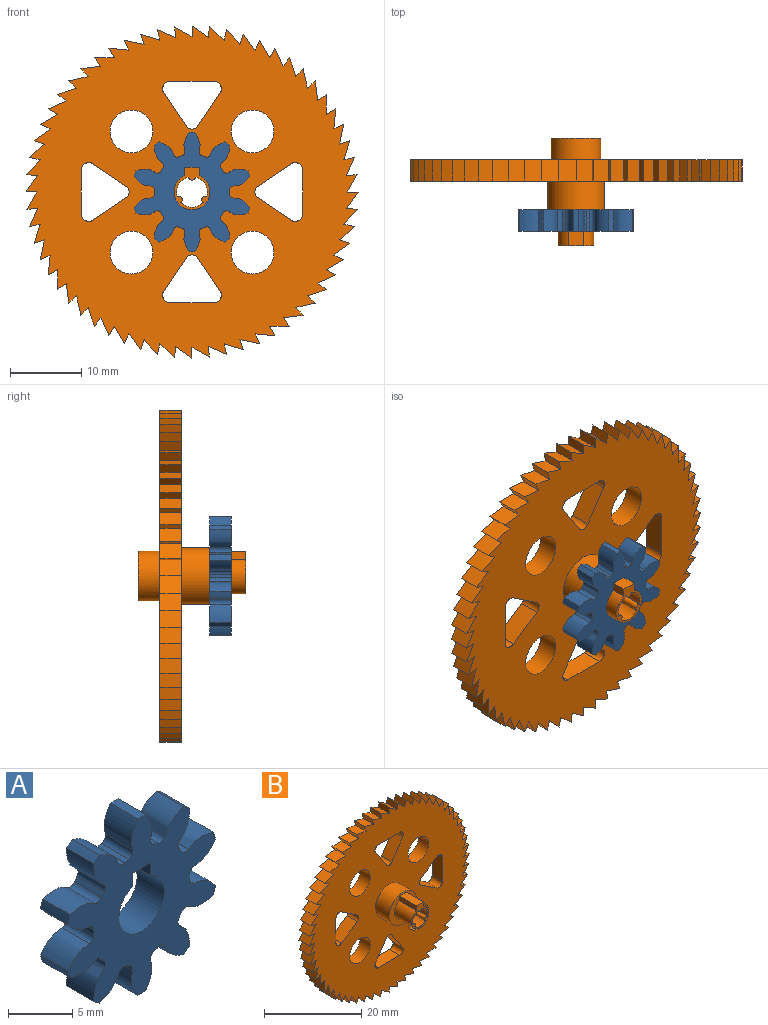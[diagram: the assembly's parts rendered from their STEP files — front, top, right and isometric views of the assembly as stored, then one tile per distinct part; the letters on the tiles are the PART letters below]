
ASSEMBLY  parts=2 mates=1
PART A: 66 faces, bbox 16.2x3x16.8 mm
  f0: cylinder r=8.4mm len=3mm, axis (0,1,0), area 2.5mm2, adj f9,f15,f56,f63
  f1: cylinder r=8.4mm len=3mm, axis (0,1,0), area 2.5mm2, adj f9,f15,f16,f58
  f2: cylinder r=8.4mm len=3mm, axis (0,1,0), area 2.5mm2, adj f9,f15,f46,f53
  f3: cylinder r=8.4mm len=3mm, axis (0,1,0), area 2.5mm2, adj f9,f15,f48,f61
  f4: cylinder r=8.4mm len=3mm, axis (0,1,0), area 2.5mm2, adj f9,f15,f36,f43
  f5: cylinder r=8.4mm len=3mm, axis (0,1,0), area 2.5mm2, adj f9,f15,f31,f38
  f6: cylinder r=8.4mm len=3mm, axis (0,1,0), area 2.5mm2, adj f9,f15,f26,f33
  f7: cylinder r=8.4mm len=3mm, axis (0,1,0), area 2.5mm2, adj f9,f15,f28,f51
  f8: cylinder r=8.4mm len=3mm, axis (0,1,0), area 2.5mm2, adj f9,f15,f23,f41
  f9: plane 16.83x16.25mm, normal (0,-1,0), area 125.5mm2, adj f0,f1,f2,f3,f4,f5,f6,f7
  f10: plane 3x1.21mm, normal (-1,0,0), area 3.6mm2, adj f9,f11,f13,f15
  f11: cylinder r=2.5mm len=5mm, axis (0,1,0), area 41mm2, adj f9,f10,f12,f15
  f12: plane 3x1.21mm, normal (1,0,0), area 3.6mm2, adj f9,f11,f13,f15
  f13: plane 3x2mm, normal (0,0,-1), area 6mm2, adj f9,f10,f12,f15
  f14: cylinder r=8.4mm len=3mm, axis (0,1,0), area 2.5mm2, adj f9,f15,f18,f21
  f15: plane 16.83x16.25mm, normal (0,1,0), area 125.5mm2, adj f0,f1,f2,f3,f4,f5,f6,f7
  f16: extruded ~3x2.37mm, area 8.5mm2, adj f1,f9,f15,f19
  f17: cylinder r=5.25mm len=3mm, axis (0,1,0), area 1.3mm2, adj f9,f15,f19,f20
  f18: extruded ~3x2.37mm, area 8.5mm2, adj f9,f14,f15,f20
  f19: cylinder r=0.58mm len=3mm, axis (0,1,0), area 2.5mm2, adj f9,f15,f16,f17
  f20: cylinder r=0.58mm len=3mm, axis (0,1,0), area 2.5mm2, adj f9,f15,f17,f18
  f21: extruded ~3x2.73mm, area 8.5mm2, adj f9,f14,f15,f24
  f22: cylinder r=5.25mm len=3mm, axis (0,1,0), area 1.3mm2, adj f9,f15,f24,f25
  f23: extruded ~3x2.51mm, area 8.5mm2, adj f8,f9,f15,f25
  f24: cylinder r=0.58mm len=3mm, axis (0,1,0), area 2.5mm2, adj f9,f15,f21,f22
  f25: cylinder r=0.58mm len=3mm, axis (0,1,0), area 2.5mm2, adj f9,f15,f22,f23
  f26: extruded ~3x2.37mm, area 8.5mm2, adj f6,f9,f15,f29
  f27: cylinder r=5.25mm len=3mm, axis (0,1,0), area 1.3mm2, adj f9,f15,f29,f30
  f28: extruded ~3x2.37mm, area 8.5mm2, adj f7,f9,f15,f30
  f29: cylinder r=0.58mm len=3mm, axis (0,1,0), area 2.5mm2, adj f9,f15,f26,f27
  f30: cylinder r=0.58mm len=3mm, axis (0,1,0), area 2.5mm2, adj f9,f15,f27,f28
  f31: extruded ~3x2.51mm, area 8.5mm2, adj f5,f9,f15,f34
  f32: cylinder r=5.25mm len=3mm, axis (0,1,0), area 1.3mm2, adj f9,f15,f34,f35
  f33: extruded ~3x2.73mm, area 8.5mm2, adj f6,f9,f15,f35
  f34: cylinder r=0.58mm len=3mm, axis (0,1,0), area 2.5mm2, adj f9,f15,f31,f32
  f35: cylinder r=0.58mm len=3mm, axis (0,1,0), area 2.5mm2, adj f9,f15,f32,f33
  f36: extruded ~3x2.68mm, area 8.5mm2, adj f4,f9,f15,f39
  f37: cylinder r=5.25mm len=3mm, axis (0,1,0), area 1.3mm2, adj f9,f15,f39,f40
  f38: extruded ~3x2.05mm, area 8.5mm2, adj f5,f9,f15,f40
  f39: cylinder r=0.58mm len=3mm, axis (0,1,0), area 2.5mm2, adj f9,f15,f36,f37
  f40: cylinder r=0.58mm len=3mm, axis (0,1,0), area 2.5mm2, adj f9,f15,f37,f38
  f41: extruded ~3x2.05mm, area 8.5mm2, adj f8,f9,f15,f44
  f42: cylinder r=5.25mm len=3mm, axis (0,1,0), area 1.3mm2, adj f9,f15,f44,f45
  f43: extruded ~3x2.68mm, area 8.5mm2, adj f4,f9,f15,f45
  f44: cylinder r=0.58mm len=3mm, axis (0,1,0), area 2.5mm2, adj f9,f15,f41,f42
  f45: cylinder r=0.58mm len=3mm, axis (0,1,0), area 2.5mm2, adj f9,f15,f42,f43
  f46: extruded ~3x2.05mm, area 8.5mm2, adj f2,f9,f15,f49
  f47: cylinder r=5.25mm len=3mm, axis (0,1,0), area 1.3mm2, adj f9,f15,f49,f50
  f48: extruded ~3x2.68mm, area 8.5mm2, adj f3,f9,f15,f50
  f49: cylinder r=0.58mm len=3mm, axis (0,1,0), area 2.5mm2, adj f9,f15,f46,f47
  f50: cylinder r=0.58mm len=3mm, axis (0,1,0), area 2.5mm2, adj f9,f15,f47,f48
  f51: extruded ~3x2.73mm, area 8.5mm2, adj f7,f9,f15,f54
  f52: cylinder r=5.25mm len=3mm, axis (0,1,0), area 1.3mm2, adj f9,f15,f54,f55
  f53: extruded ~3x2.51mm, area 8.5mm2, adj f2,f9,f15,f55
  f54: cylinder r=0.58mm len=3mm, axis (0,1,0), area 2.5mm2, adj f9,f15,f51,f52
  f55: cylinder r=0.58mm len=3mm, axis (0,1,0), area 2.5mm2, adj f9,f15,f52,f53
  f56: extruded ~3x2.51mm, area 8.5mm2, adj f0,f9,f15,f59
  f57: cylinder r=5.25mm len=3mm, axis (0,1,0), area 1.3mm2, adj f9,f15,f59,f60
  f58: extruded ~3x2.73mm, area 8.5mm2, adj f1,f9,f15,f60
  f59: cylinder r=0.58mm len=3mm, axis (0,1,0), area 2.5mm2, adj f9,f15,f56,f57
  f60: cylinder r=0.58mm len=3mm, axis (0,1,0), area 2.5mm2, adj f9,f15,f57,f58
  f61: extruded ~3x2.68mm, area 8.5mm2, adj f3,f9,f15,f64
  f62: cylinder r=5.25mm len=3mm, axis (0,1,0), area 1.3mm2, adj f9,f15,f64,f65
  f63: extruded ~3x2.05mm, area 8.5mm2, adj f0,f9,f15,f65
  f64: cylinder r=0.58mm len=3mm, axis (0,1,0), area 2.5mm2, adj f9,f15,f61,f62
  f65: cylinder r=0.58mm len=3mm, axis (0,1,0), area 2.5mm2, adj f9,f15,f62,f63
PART B: 165 faces, bbox 46.5x15x46.5 mm
  f0: plane 46.5x46.5mm, normal (0,-1,0), area 1281.1mm2, adj f2,f3,f4,f5,f6,f7,f8,f9
  f1: plane 46.5x46.5mm, normal (0,1,0), area 1292.9mm2, adj f2,f3,f4,f5,f6,f7,f8,f9
  f2: plane 3x1.49mm, normal (-0.99,0,0.1), area 4.5mm2, adj f0,f1,f3,f121
  f3: plane 3x2.27mm, normal (0.58,0,0.81), area 8.4mm2, adj f0,f1,f2,f4
  f4: plane 3x1.5mm, normal (-1,0,0), area 4.5mm2, adj f0,f1,f3,f5
  f5: plane 3x2.43mm, normal (0.49,0,0.87), area 8.4mm2, adj f0,f1,f4,f6
  f6: plane 3x1.49mm, normal (-0.99,0,-0.1), area 4.5mm2, adj f0,f1,f5,f7
  f7: plane 3x2.56mm, normal (0.4,0,0.92), area 8.4mm2, adj f0,f1,f6,f8
  f8: plane 3x1.47mm, normal (-0.98,0,-0.21), area 4.5mm2, adj f0,f1,f7,f9
  f9: plane 3x2.66mm, normal (0.3,0,0.95), area 8.4mm2, adj f0,f1,f8,f10
  f10: plane 3x1.43mm, normal (-0.95,0,-0.31), area 4.5mm2, adj f0,f1,f9,f11
  f11: plane 3x2.74mm, normal (0.2,0,0.98), area 8.4mm2, adj f0,f1,f10,f12
  f12: plane 3x1.37mm, normal (-0.91,0,-0.41), area 4.5mm2, adj f0,f1,f11,f13
  f13: plane 3x2.78mm, normal (0.1,0,1), area 8.4mm2, adj f0,f1,f12,f14
  f14: plane 3x1.3mm, normal (-0.87,0,-0.5), area 4.5mm2, adj f0,f1,f13,f15
  f15: plane 3x2.79mm, normal (-0.01,0,1), area 8.4mm2, adj f0,f1,f14,f16
  f16: plane 3x1.21mm, normal (-0.81,0,-0.59), area 4.5mm2, adj f0,f1,f15,f17
  f17: plane 3x2.77mm, normal (-0.11,0,0.99), area 8.4mm2, adj f0,f1,f16,f18
  f18: plane 3x1.11mm, normal (-0.74,0,-0.67), area 4.5mm2, adj f0,f1,f17,f19
  f19: plane 3x2.72mm, normal (-0.22,0,0.98), area 8.4mm2, adj f0,f1,f18,f20
  f20: plane 3x1.11mm, normal (-0.67,0,-0.74), area 4.5mm2, adj f0,f1,f19,f21
  f21: plane 3x2.65mm, normal (-0.32,0,0.95), area 8.4mm2, adj f0,f1,f20,f22
  f22: plane 3x1.21mm, normal (-0.59,0,-0.81), area 4.5mm2, adj f0,f1,f21,f23
  f23: plane 3x2.54mm, normal (-0.42,0,0.91), area 8.4mm2, adj f0,f1,f22,f24
  f24: plane 3x1.3mm, normal (-0.5,0,-0.87), area 4.5mm2, adj f0,f1,f23,f25
  f25: plane 3x2.4mm, normal (-0.51,0,0.86), area 8.4mm2, adj f0,f1,f24,f26
  f26: plane 3x1.37mm, normal (-0.41,0,-0.91), area 4.5mm2, adj f0,f1,f25,f27
  f27: plane 3x2.24mm, normal (-0.6,0,0.8), area 8.4mm2, adj f0,f1,f26,f28
  f28: plane 3x1.43mm, normal (-0.31,0,-0.95), area 4.5mm2, adj f0,f1,f27,f29
  f29: plane 3x2.06mm, normal (-0.68,0,0.74), area 8.4mm2, adj f0,f1,f28,f30
  f30: plane 3x1.47mm, normal (-0.21,0,-0.98), area 4.5mm2, adj f0,f1,f29,f31
  f31: plane 3x2.09mm, normal (-0.75,0,0.66), area 8.4mm2, adj f0,f1,f30,f32
  f32: plane 3x1.49mm, normal (-0.1,0,-0.99), area 4.5mm2, adj f0,f1,f31,f33
  f33: plane 3x2.27mm, normal (-0.81,0,0.58), area 8.4mm2, adj f0,f1,f32,f34
  f34: plane 3x1.5mm, normal (0,0,-1), area 4.5mm2, adj f0,f1,f33,f35
  f35: plane 3x2.43mm, normal (-0.87,0,0.49), area 8.4mm2, adj f0,f1,f34,f36
  f36: plane 3x1.49mm, normal (0.1,0,-0.99), area 4.5mm2, adj f0,f1,f35,f37
  f37: plane 3x2.56mm, normal (-0.92,0,0.4), area 8.4mm2, adj f0,f1,f36,f38
  f38: plane 3x1.47mm, normal (0.21,0,-0.98), area 4.5mm2, adj f0,f1,f37,f39
  f39: plane 3x2.66mm, normal (-0.95,0,0.3), area 8.4mm2, adj f0,f1,f38,f40
  f40: plane 3x1.43mm, normal (0.31,0,-0.95), area 4.5mm2, adj f0,f1,f39,f41
  f41: plane 3x2.74mm, normal (-0.98,0,0.2), area 8.4mm2, adj f0,f1,f40,f42
  f42: plane 3x1.37mm, normal (0.41,0,-0.91), area 4.5mm2, adj f0,f1,f41,f43
  f43: plane 3x2.78mm, normal (-1,0,0.1), area 8.4mm2, adj f0,f1,f42,f44
  f44: plane 3x1.3mm, normal (0.5,0,-0.87), area 4.5mm2, adj f0,f1,f43,f45
  f45: plane 3x2.79mm, normal (-1,0,-0.01), area 8.4mm2, adj f0,f1,f44,f46
  f46: plane 3x1.21mm, normal (0.59,0,-0.81), area 4.5mm2, adj f0,f1,f45,f47
  f47: plane 3x2.77mm, normal (-0.99,0,-0.11), area 8.4mm2, adj f0,f1,f46,f48
  f48: plane 3x1.11mm, normal (0.67,0,-0.74), area 4.5mm2, adj f0,f1,f47,f49
  f49: plane 3x2.72mm, normal (-0.98,0,-0.22), area 8.4mm2, adj f0,f1,f48,f50
  f50: plane 3x1.11mm, normal (0.74,0,-0.67), area 4.5mm2, adj f0,f1,f49,f51
  f51: plane 3x2.65mm, normal (-0.95,0,-0.32), area 8.4mm2, adj f0,f1,f50,f52
  f52: plane 3x1.21mm, normal (0.81,0,-0.59), area 4.5mm2, adj f0,f1,f51,f53
  f53: plane 3x2.54mm, normal (-0.91,0,-0.42), area 8.4mm2, adj f0,f1,f52,f54
  f54: plane 3x1.3mm, normal (0.87,0,-0.5), area 4.5mm2, adj f0,f1,f53,f55
  f55: plane 3x2.4mm, normal (-0.86,0,-0.51), area 8.4mm2, adj f0,f1,f54,f56
  f56: plane 3x1.37mm, normal (0.91,0,-0.41), area 4.5mm2, adj f0,f1,f55,f57
  f57: plane 3x2.24mm, normal (-0.8,0,-0.6), area 8.4mm2, adj f0,f1,f56,f58
  f58: plane 3x1.43mm, normal (0.95,0,-0.31), area 4.5mm2, adj f0,f1,f57,f59
  f59: plane 3x2.06mm, normal (-0.74,0,-0.68), area 8.4mm2, adj f0,f1,f58,f60
  f60: plane 3x1.47mm, normal (0.98,0,-0.21), area 4.5mm2, adj f0,f1,f59,f61
  f61: plane 3x2.09mm, normal (-0.66,0,-0.75), area 8.4mm2, adj f0,f1,f60,f62
  f62: plane 3x1.49mm, normal (0.99,0,-0.1), area 4.5mm2, adj f0,f1,f61,f63
  f63: plane 3x2.27mm, normal (-0.58,0,-0.81), area 8.4mm2, adj f0,f1,f62,f64
  f64: plane 3x1.5mm, normal (1,0,0), area 4.5mm2, adj f0,f1,f63,f65
  f65: plane 3x2.43mm, normal (-0.49,0,-0.87), area 8.4mm2, adj f0,f1,f64,f66
  f66: plane 3x1.49mm, normal (0.99,0,0.1), area 4.5mm2, adj f0,f1,f65,f67
  f67: plane 3x2.56mm, normal (-0.4,0,-0.92), area 8.4mm2, adj f0,f1,f66,f68
  f68: plane 3x1.47mm, normal (0.98,0,0.21), area 4.5mm2, adj f0,f1,f67,f69
  f69: plane 3x2.66mm, normal (-0.3,0,-0.95), area 8.4mm2, adj f0,f1,f68,f70
  f70: plane 3x1.43mm, normal (0.95,0,0.31), area 4.5mm2, adj f0,f1,f69,f71
  f71: plane 3x2.74mm, normal (-0.2,0,-0.98), area 8.4mm2, adj f0,f1,f70,f72
  f72: plane 3x1.37mm, normal (0.91,0,0.41), area 4.5mm2, adj f0,f1,f71,f73
  f73: plane 3x2.78mm, normal (-0.1,0,-1), area 8.4mm2, adj f0,f1,f72,f74
  f74: plane 3x1.3mm, normal (0.87,0,0.5), area 4.5mm2, adj f0,f1,f73,f75
  f75: plane 3x2.79mm, normal (0.01,0,-1), area 8.4mm2, adj f0,f1,f74,f76
  f76: plane 3x1.21mm, normal (0.81,0,0.59), area 4.5mm2, adj f0,f1,f75,f77
  f77: plane 3x2.77mm, normal (0.11,0,-0.99), area 8.4mm2, adj f0,f1,f76,f78
  f78: plane 3x1.11mm, normal (0.74,0,0.67), area 4.5mm2, adj f0,f1,f77,f79
  f79: plane 3x2.72mm, normal (0.22,0,-0.98), area 8.4mm2, adj f0,f1,f78,f80
  f80: plane 3x1.11mm, normal (0.67,0,0.74), area 4.5mm2, adj f0,f1,f79,f81
  f81: plane 3x2.65mm, normal (0.32,0,-0.95), area 8.4mm2, adj f0,f1,f80,f82
  f82: plane 3x1.21mm, normal (0.59,0,0.81), area 4.5mm2, adj f0,f1,f81,f83
  f83: plane 3x2.54mm, normal (0.42,0,-0.91), area 8.4mm2, adj f0,f1,f82,f84
  f84: plane 3x1.3mm, normal (0.5,0,0.87), area 4.5mm2, adj f0,f1,f83,f85
  f85: plane 3x2.4mm, normal (0.51,0,-0.86), area 8.4mm2, adj f0,f1,f84,f86
  f86: plane 3x1.37mm, normal (0.41,0,0.91), area 4.5mm2, adj f0,f1,f85,f87
  f87: plane 3x2.24mm, normal (0.6,0,-0.8), area 8.4mm2, adj f0,f1,f86,f88
  f88: plane 3x1.43mm, normal (0.31,0,0.95), area 4.5mm2, adj f0,f1,f87,f89
  f89: plane 3x2.06mm, normal (0.68,0,-0.74), area 8.4mm2, adj f0,f1,f88,f90
  f90: plane 3x1.47mm, normal (0.21,0,0.98), area 4.5mm2, adj f0,f1,f89,f91
  f91: plane 3x2.09mm, normal (0.75,0,-0.66), area 8.4mm2, adj f0,f1,f90,f92
  f92: plane 3x1.49mm, normal (0.1,0,0.99), area 4.5mm2, adj f0,f1,f91,f93
  f93: plane 3x2.27mm, normal (0.81,0,-0.58), area 8.4mm2, adj f0,f1,f92,f94
  f94: plane 3x1.5mm, normal (0,0,1), area 4.5mm2, adj f0,f1,f93,f95
  f95: plane 3x2.43mm, normal (0.87,0,-0.49), area 8.4mm2, adj f0,f1,f94,f96
  f96: plane 3x1.49mm, normal (-0.1,0,0.99), area 4.5mm2, adj f0,f1,f95,f97
  f97: plane 3x2.56mm, normal (0.92,0,-0.4), area 8.4mm2, adj f0,f1,f96,f98
  f98: plane 3x1.47mm, normal (-0.21,0,0.98), area 4.5mm2, adj f0,f1,f97,f99
  f99: plane 3x2.66mm, normal (0.95,0,-0.3), area 8.4mm2, adj f0,f1,f98,f100
  f100: plane 3x1.43mm, normal (-0.31,0,0.95), area 4.5mm2, adj f0,f1,f99,f101
  f101: plane 3x2.74mm, normal (0.98,0,-0.2), area 8.4mm2, adj f0,f1,f100,f102
  f102: plane 3x1.37mm, normal (-0.41,0,0.91), area 4.5mm2, adj f0,f1,f101,f103
  f103: plane 3x2.78mm, normal (1,0,-0.1), area 8.4mm2, adj f0,f1,f102,f104
  f104: plane 3x1.3mm, normal (-0.5,0,0.87), area 4.5mm2, adj f0,f1,f103,f105
  f105: plane 3x2.79mm, normal (1,0,0.01), area 8.4mm2, adj f0,f1,f104,f106
  f106: plane 3x1.21mm, normal (-0.59,0,0.81), area 4.5mm2, adj f0,f1,f105,f107
  f107: plane 3x2.77mm, normal (0.99,0,0.11), area 8.4mm2, adj f0,f1,f106,f108
  f108: plane 3x1.11mm, normal (-0.67,0,0.74), area 4.5mm2, adj f0,f1,f107,f109
  f109: plane 3x2.72mm, normal (0.98,0,0.22), area 8.4mm2, adj f0,f1,f108,f110
  f110: plane 3x1.11mm, normal (-0.74,0,0.67), area 4.5mm2, adj f0,f1,f109,f111
  f111: plane 3x2.65mm, normal (0.95,0,0.32), area 8.4mm2, adj f0,f1,f110,f112
  f112: plane 3x1.21mm, normal (-0.81,0,0.59), area 4.5mm2, adj f0,f1,f111,f113
  f113: plane 3x2.54mm, normal (0.91,0,0.42), area 8.4mm2, adj f0,f1,f112,f114
  f114: plane 3x1.3mm, normal (-0.87,0,0.5), area 4.5mm2, adj f0,f1,f113,f115
  f115: plane 3x2.4mm, normal (0.86,0,0.51), area 8.4mm2, adj f0,f1,f114,f116
  f116: plane 3x1.37mm, normal (-0.91,0,0.41), area 4.5mm2, adj f0,f1,f115,f117
  f117: plane 3x2.24mm, normal (0.8,0,0.6), area 8.4mm2, adj f0,f1,f116,f118
  f118: plane 3x1.43mm, normal (-0.95,0,0.31), area 4.5mm2, adj f0,f1,f117,f119
  f119: plane 3x2.06mm, normal (0.74,0,0.68), area 8.4mm2, adj f0,f1,f118,f120
  f120: plane 3x1.47mm, normal (-0.98,0,0.21), area 4.5mm2, adj f0,f1,f119,f121
  f121: plane 3x2.09mm, normal (0.66,0,0.75), area 8.4mm2, adj f0,f1,f2,f120
  f122: cylinder r=0.5mm len=15mm, axis (0,-1,0), area 21.8mm2, adj f123,f127,f129,f136
  f123: cylinder r=2.15mm len=15mm, axis (0,-1,0), area 52.5mm2, adj f122,f124,f129,f136
  f124: cylinder r=0.5mm len=15mm, axis (0,-1,0), area 21.8mm2, adj f123,f125,f129,f136
  f125: cylinder r=2.15mm len=15mm, axis (0,-1,0), area 52.5mm2, adj f124,f126,f129,f136
  f126: cylinder r=0.5mm len=15mm, axis (0,-1,0), area 21.8mm2, adj f125,f127,f129,f136
  f127: cylinder r=2.15mm len=15mm, axis (0,-1,0), area 52.5mm2, adj f122,f126,f129,f136
  f128: cylinder r=3.5mm len=7mm, axis (0,-1,0), area 66mm2, adj f1,f129
  f129: plane 7x7mm, normal (0,1,0), area 25.1mm2, adj f122,f123,f124,f125,f126,f127,f128
  f130: cylinder r=4mm len=8mm, axis (0,1,0), area 100.5mm2, adj f0,f131
  f131: plane 8x8mm, normal (0,-1,0), area 28.5mm2, adj f130,f132,f133,f134,f135
  f132: plane 5x1.21mm, normal (-1,0,0), area 6mm2, adj f131,f133,f135,f136
  f133: cylinder r=2.5mm len=5mm, axis (0,1,0), area 68.3mm2, adj f131,f132,f134,f136
  f134: plane 5x1.21mm, normal (1,0,0), area 6mm2, adj f131,f133,f135,f136
  f135: plane 5x2mm, normal (0,0,1), area 10mm2, adj f131,f132,f134,f136
  f136: plane 6x5mm, normal (0,-1,0), area 8.4mm2, adj f122,f123,f124,f125,f126,f127,f132,f133
  f137: plane 6.26x3mm, normal (0,0,-1), area 18.8mm2, adj f0,f1,f162,f164
  f138: plane 4.68x3.13mm, normal (0.83,0,0.56), area 16.9mm2, adj f0,f1,f163,f164
  f139: plane 4.68x3.13mm, normal (-0.83,0,0.56), area 16.9mm2, adj f0,f1,f162,f163
  f140: cylinder r=3mm len=6mm, axis (0,-1,0), area 56.5mm2, adj f0,f1
  f141: plane 4.68x3.13mm, normal (0.56,0,0.83), area 16.9mm2, adj f0,f1,f153,f155
  f142: plane 6.26x3mm, normal (-1,0,0), area 18.8mm2, adj f0,f1,f154,f155
  f143: plane 4.68x3.13mm, normal (0.56,0,-0.83), area 16.9mm2, adj f0,f1,f153,f154
  f144: cylinder r=3mm len=6mm, axis (0,-1,0), area 56.5mm2, adj f0,f1
  f145: cylinder r=3mm len=6mm, axis (0,-1,0), area 56.5mm2, adj f0,f1
  f146: plane 4.68x3.13mm, normal (-0.56,0,-0.83), area 16.9mm2, adj f0,f1,f159,f161
  f147: plane 6.26x3mm, normal (1,0,0), area 18.8mm2, adj f0,f1,f160,f161
  f148: plane 4.68x3.13mm, normal (-0.56,0,0.83), area 16.9mm2, adj f0,f1,f159,f160
  f149: cylinder r=3mm len=6mm, axis (0,-1,0), area 56.5mm2, adj f0,f1
  f150: plane 4.68x3.13mm, normal (0.83,0,-0.56), area 16.9mm2, adj f0,f1,f156,f158
  f151: plane 6.26x3mm, normal (0,0,1), area 18.8mm2, adj f0,f1,f157,f158
  f152: plane 4.68x3.13mm, normal (-0.83,0,-0.56), area 16.9mm2, adj f0,f1,f156,f157
  f153: cylinder r=1mm len=3mm, axis (0,1,0), area 5.9mm2, adj f0,f1,f141,f143
  f154: cylinder r=1mm len=3mm, axis (0,1,0), area 6.5mm2, adj f0,f1,f142,f143
  f155: cylinder r=1mm len=3mm, axis (0,1,0), area 6.5mm2, adj f0,f1,f141,f142
  f156: cylinder r=1mm len=3mm, axis (0,1,0), area 5.9mm2, adj f0,f1,f150,f152
  f157: cylinder r=1mm len=3mm, axis (0,1,0), area 6.5mm2, adj f0,f1,f151,f152
  f158: cylinder r=1mm len=3mm, axis (0,1,0), area 6.5mm2, adj f0,f1,f150,f151
  f159: cylinder r=1mm len=3mm, axis (0,1,0), area 5.9mm2, adj f0,f1,f146,f148
  f160: cylinder r=1mm len=3mm, axis (0,1,0), area 6.5mm2, adj f0,f1,f147,f148
  f161: cylinder r=1mm len=3mm, axis (0,1,0), area 6.5mm2, adj f0,f1,f146,f147
  f162: cylinder r=1mm len=3mm, axis (0,1,0), area 6.5mm2, adj f0,f1,f137,f139
  f163: cylinder r=1mm len=3mm, axis (0,1,0), area 5.9mm2, adj f0,f1,f138,f139
  f164: cylinder r=1mm len=3mm, axis (0,1,0), area 6.5mm2, adj f0,f1,f137,f138
PLACE A t=(0,-7,0)mm
PLACE B at identity fixed
MATE fastened B.f135 <-> A.f13  axis (0,0,1) through (-1,-7,3.5)mm
